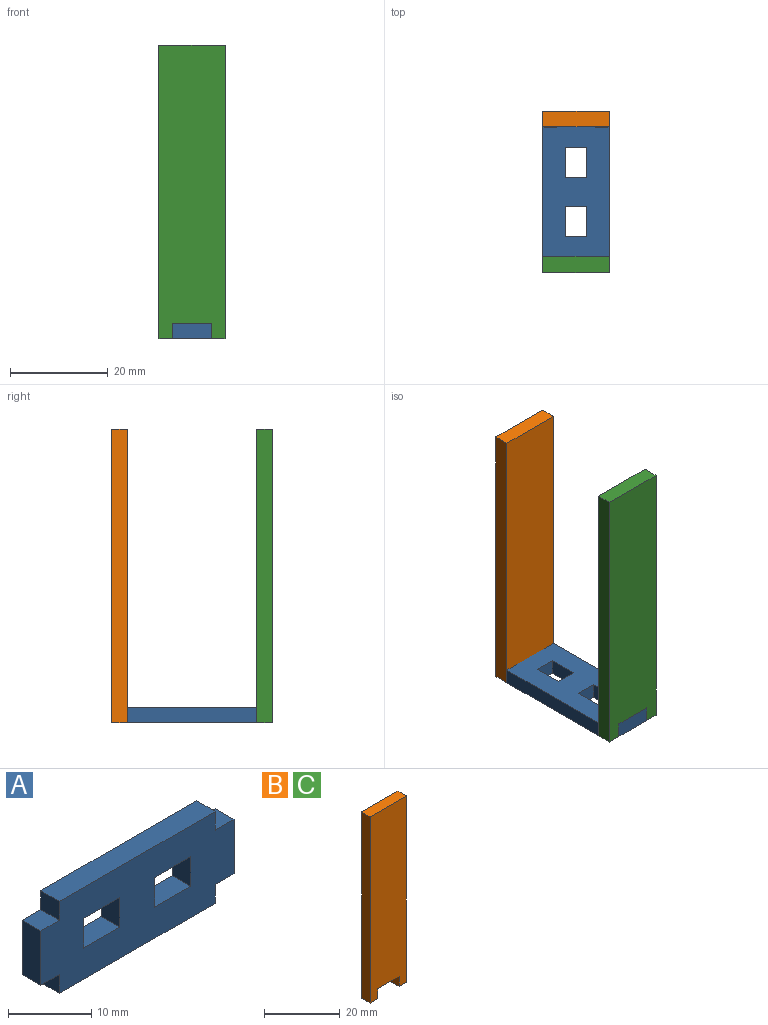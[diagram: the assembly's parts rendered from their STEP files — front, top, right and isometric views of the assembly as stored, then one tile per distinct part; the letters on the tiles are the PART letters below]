
ASSEMBLY  parts=3 mates=1
PART A: 22 faces, bbox 32.8x3.2x13.5 mm
  f0: plane 6.15x3.18mm, normal (0,0,-1), area 19.5mm2, adj f1,f19,f20,f21
  f1: plane 4.35x3.18mm, normal (-1,0,0), area 13.8mm2, adj f0,f2,f20,f21
  f2: plane 6.15x3.18mm, normal (0,0,1), area 19.5mm2, adj f1,f19,f20,f21
  f3: plane 4.35x3.18mm, normal (1,0,0), area 13.8mm2, adj f4,f17,f20,f21
  f4: plane 6.15x3.18mm, normal (0,0,-1), area 19.5mm2, adj f3,f5,f20,f21
  f5: plane 4.35x3.18mm, normal (-1,0,0), area 13.8mm2, adj f4,f17,f20,f21
  f6: plane 3.18x2.75mm, normal (1,0,0), area 8.7mm2, adj f7,f18,f20,f21
  f7: plane 3.18x3.18mm, normal (0,0,-1), area 10.1mm2, adj f6,f8,f20,f21
  f8: plane 8x3.18mm, normal (1,0,0), area 25.4mm2, adj f7,f9,f20,f21
  f9: plane 3.18x3.18mm, normal (0,0,1), area 10.1mm2, adj f8,f10,f20,f21
  f10: plane 3.18x2.75mm, normal (1,0,0), area 8.7mm2, adj f9,f11,f20,f21
  f11: plane 26.49x3.18mm, normal (0,0,1), area 84.1mm2, adj f10,f12,f20,f21
  f12: plane 3.18x2.75mm, normal (-1,0,0), area 8.7mm2, adj f11,f13,f20,f21
  f13: plane 3.18x3.18mm, normal (0,0,1), area 10.1mm2, adj f12,f14,f20,f21
  f14: plane 8x3.18mm, normal (-1,0,0), area 25.4mm2, adj f13,f15,f20,f21
  f15: plane 3.18x3.18mm, normal (0,0,-1), area 10.1mm2, adj f14,f16,f20,f21
  f16: plane 3.18x2.75mm, normal (-1,0,0), area 8.7mm2, adj f15,f18,f20,f21
  f17: plane 6.15x3.18mm, normal (0,0,1), area 19.5mm2, adj f3,f5,f20,f21
  f18: plane 26.49x3.18mm, normal (0,0,-1), area 84.1mm2, adj f6,f16,f20,f21
  f19: plane 4.35x3.18mm, normal (1,0,0), area 13.8mm2, adj f0,f2,f20,f21
  f20: plane 32.84x13.5mm, normal (0,-1,0), area 354.9mm2, adj f0,f1,f2,f3,f4,f5,f6,f7
  f21: plane 32.84x13.5mm, normal (0,1,0), area 354.9mm2, adj f0,f1,f2,f3,f4,f5,f6,f7
PART B: 10 faces, bbox 13.5x3.2x60 mm
  f0: plane 8x3.18mm, normal (0,0,-1), area 25.4mm2, adj f4,f5,f7,f9
  f1: plane 60x3.18mm, normal (1,0,0), area 190.5mm2, adj f2,f4,f5,f6
  f2: plane 13.5x3.18mm, normal (0,0,1), area 42.9mm2, adj f1,f3,f4,f5
  f3: plane 60x3.18mm, normal (-1,0,0), area 190.5mm2, adj f2,f4,f5,f8
  f4: plane 60x13.5mm, normal (0,-1,0), area 784.6mm2, adj f0,f1,f2,f3,f6,f7,f8,f9
  f5: plane 60x13.5mm, normal (0,1,0), area 784.6mm2, adj f0,f1,f2,f3,f6,f7,f8,f9
  f6: plane 3.18x2.75mm, normal (0,0,-1), area 8.7mm2, adj f1,f4,f5,f7
  f7: plane 3.18x3.18mm, normal (-1,0,0), area 10.1mm2, adj f0,f4,f5,f6
  f8: plane 3.18x2.75mm, normal (0,0,-1), area 8.7mm2, adj f3,f4,f5,f9
  f9: plane 3.18x3.18mm, normal (1,0,0), area 10.1mm2, adj f0,f4,f5,f8
PART C: same geometry as B
PLACE A rot(axis=(-0.58,0.58,-0.58),120deg) t=(-7.64,16.42,-30.03)mm
PLACE B t=(-7.64,26.82,-0.03)mm
PLACE C t=(-7.64,-2.85,-0.03)mm
MATE parallel A.f9 <-> C.f7  axis (1,0,0) through (-3.64,-4.43,-28.45)mm
